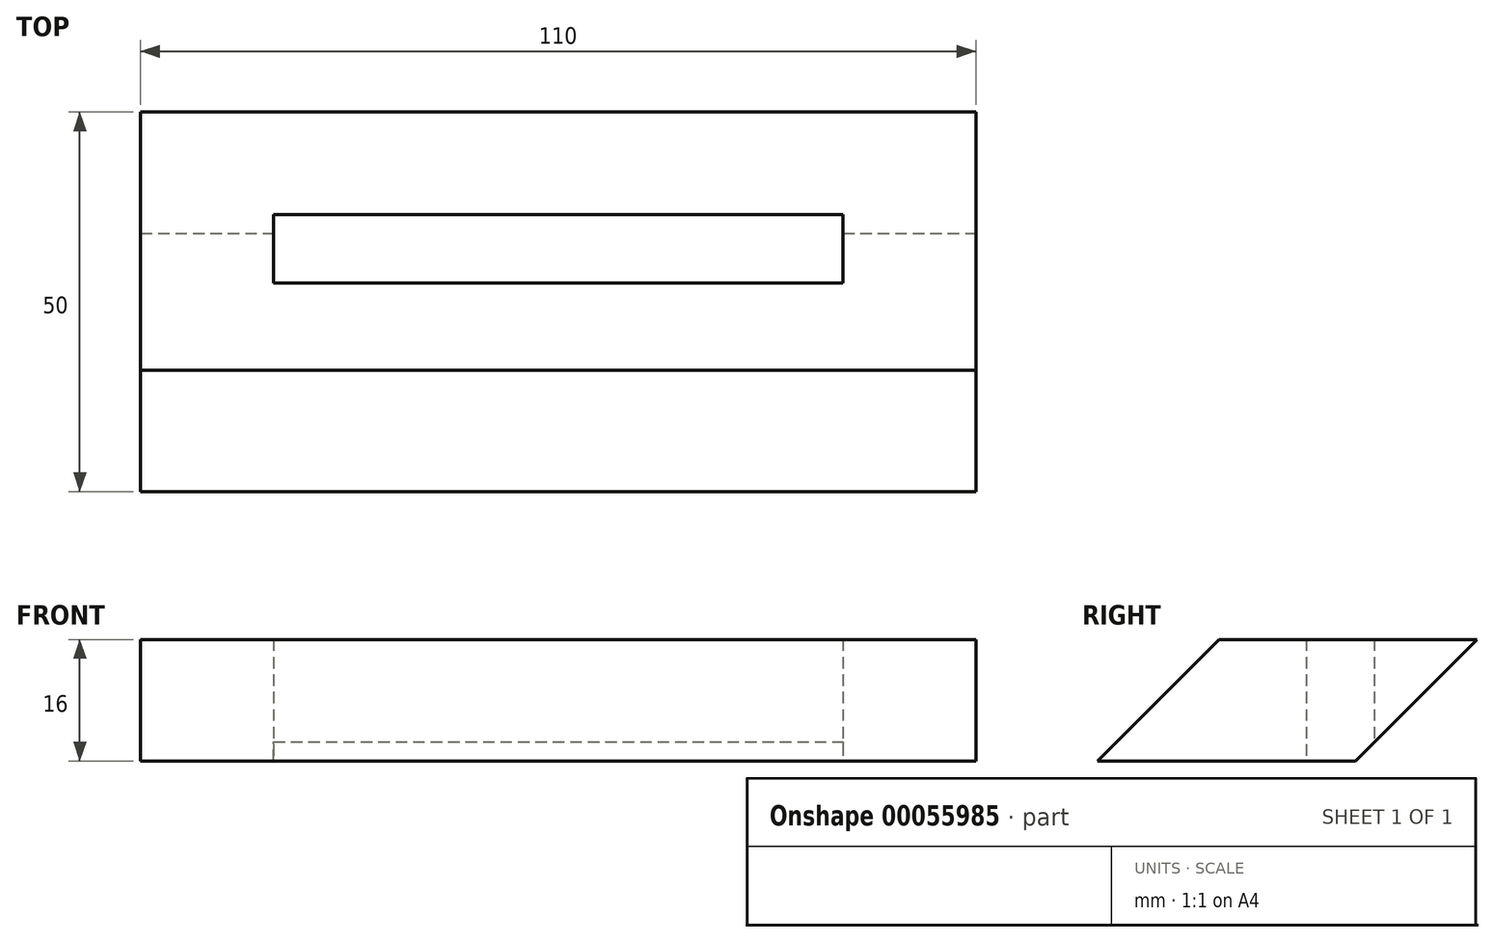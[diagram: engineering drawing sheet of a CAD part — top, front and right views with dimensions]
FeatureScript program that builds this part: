
annotation { "Feature Type Name" : "Feature", "Feature Type Description" : "" }
export const myFeature = defineFeature(function(context is Context, id is Id, definition is map)
    precondition{}
    {
        {
            var Q0;
            Q0=qCreatedBy(makeId("Top.planeOp"),FACE);
            var sketch = newSketch(context, id + "F0", { "sketchPlane" : qUnion([Q0])});
            skLineSegment(sketch, "E0.bottom", {"start": v(0, 0) * mm, "end": v(110, 0) * mm});
            skLineSegment(sketch, "E0.top", {"start": v(0, 50) * mm, "end": v(110, 50) * mm});
            skLineSegment(sketch, "E0.left", {"start": v(0, 0) * mm, "end": v(0, 50) * mm});
            skLineSegment(sketch, "E0.right", {"start": v(110, 0) * mm, "end": v(110, 50) * mm});
            skPoint(sketch, "E1.endSnap0", {"position": v(55, 0) * mm});
            skLineSegment(sketch, "E2", {"start": v(55, 36.5) * mm, "end": v(92.5, 36.5) * mm});
            skLineSegment(sketch, "E3", {"start": v(92.5, 36.5) * mm, "end": v(92.5, 27.5) * mm});
            skLineSegment(sketch, "E4", {"start": v(55, 36.5) * mm, "end": v(17.5, 36.5) * mm});
            skLineSegment(sketch, "E5", {"start": v(17.5, 36.5) * mm, "end": v(17.5, 27.5) * mm});
            skLineSegment(sketch, "E6", {"start": v(17.5, 27.5) * mm, "end": v(92.5, 27.5) * mm});
            skSolve(sketch);
        }
        {
            var Q0;
            Q0=makeQuery(id+"F0.imprint","IMPRINT",FACE,{"disambiguationData":[TD([[makeQuery(id+"F0.imprint","IMPRINT",EDGE,{"derivedFrom":sQuery(id+"F0.wireOp",EDGE,"E0.bottom")}),1.0]])]});
            extrude(context, id + "F1", {"entities" : qUnion([Q0]), "depth" : 16 * mm});
        }
        {
            var Q0;
            Q0=makeQuery(id+"F1.opExtrude","CAP_EDGE",EDGE,{"disambiguationData":[OSD([sQuery(id+"F0.wireOp",EDGE,"E0.bottom")])],"isStart":false});
            chamfer(context, id + "F2", {"entities" : qUnion([Q0]), "width" : 16 * mm, "tangentPropagation" : true});
        }
        {
            var Q0;
            Q0=makeQuery(id+"F1.opExtrude","CAP_EDGE",EDGE,{"disambiguationData":[OSD([sQuery(id+"F0.wireOp",EDGE,"E0.top")])],"isStart":true});
            chamfer(context, id + "F3", {"entities" : qUnion([Q0]), "width" : 16 * mm, "tangentPropagation" : true});
        }
    });
